# Revit family: O2DMZD - Linked Data
name_source: partatom
category: Mechanical Equipment
units: mm (PartAtom-declared; Revit-internal decimal feet)

## family parameters
Always vertical = No
Cut with Voids When Loaded = No
OmniClass Number = 23.40.40.11.17
OmniClass Title = Refrigerated Cases
Part Type = Breaks Into
Room Calculation Point = No
Round Connector Dimension = Use Radius
Shared = Yes
Work Plane-Based = Yes

## types (4) — shared parameters
14" Shelf = Yes
BOTTOM ELECTRICAL = Yes
BOTTOM REFRIGERATION PIPING = Yes
Certifications = NSF 7, UL471, CSA
DATE = 03/29/2016
DRAIN LINE = 36"
DRAIN PIPING = Yes
Default Elevation = 48"
Description = Multi-Deck Merchandiser
EQUIPMENT DESCRIPTION = Multi-Deck Merchandiser
EQUIPMENT MARK = O2DMZD - 5 BF
GLASS = Glass
Height = 43 1/2"
High Efficiency Amps = 0 A
High Power (Cornice) Amps = 0 A
How Many Defrosts Per Day = 1
Island BTUH Conventional = 215
Island BTUH Parallel = 210
Island Discharge Air Velocity (FPM) = 50 FPM
Island Discharge Air(°F) = -1 °F
Island Electric Fail-Safe = 45 (Min)
Island Electric Termination Temp (F°) = 48 °F
Island Evaporator (°F) = -17 °F
Island Hot Gas Fail-Safe (Min) = 30 (Min)
Island Hot Gas Termination Temp (F°) = 60 °F
Island Run-Off Time (Min) = 8-10 (Min)
Island Superheat @ Bulb Set Point (°F) = 3-5 °F
Item Description = Multi-Deck Merchandiser
LF STD END = Yes
Legend Number = O2DMZD - 5 BF
Manufacturer = HILL PHOENIX
Model = O2DMZD - 5 BF
PAINTED METAL UPPER SHELF = PAINTED SHELVES
REFRIGERATION PIPING = COPPER PIPE
RT STD END = Yes
Refgn = 22 1/2"
Standard Power Amps = 0 A
URL = http://www.hillphoenix.com
Width = 41 7/8"
door position = 0"

## per-type parameters (varying)
| type | Anti-Condensate Heaters Amps | Anti-Condensate Heaters Watts | CENTER LINE | Defrost (Phase 1) 208 V Amps | Defrost (Phase 1) 208 V Watts | Defrost (Phase 1) 240 V Amps | Defrost (Phase 1) 240 V Watts | Defrost (Phase 3) 208 V Amps | Defrost (Phase 3) 208 V Watts | Defrost (Phase 3) 240 V Amps | Defrost (Phase 3) 240 V Watts | Door | High Efficiency Watts | High Power (Cornice) Watts | Length | Light Length | Lights Per Row | Number of Fans | Standard Power Watts |
| 04' | 0 A | 44 W | 24" | 807 A | 1800 W | 10 A | 2400 W | 9 A | 1800 W | 10 A | 2400 W | O2DMZD - 4' : 4' | 22 W | 26 W | 48" | 60" | 1 | 2 | 14 W |
| 06' | 0 A | 44 W | 36" | 807 A | 1800 W | 10 A | 2400 W | 9 A | 1800 W | 10 A | 2400 W | O2DMZD - 6' : 4' | 22 W | 26 W | 72" | 60" | 1 | 2 | 14 W |
| 08' | 1 A | 90 W | 48" | 12 A | 2400 W | 13 A | 3195 W | 12 A | 2400 W | 13 A | 3195 W | O2DMZD - 8' : 4' | 22 W | 30 W | 96" | 36" | 2 | 2 | 17 W |
| 12' | 1 A | 134 W | 72" | 17 A | 3600 W | 20 A | 4795 W | 17 A | 3600 W | 20 A | 4795 W | O2DMZD - doors 12' : 4' | 33 W | 53 W | 144" | 60" | 2 | 3 | 29 W |

## geometry (parser evidence)
native form markers: Blend x10, Sweep x12
no freeform markers — native parametric forms only
